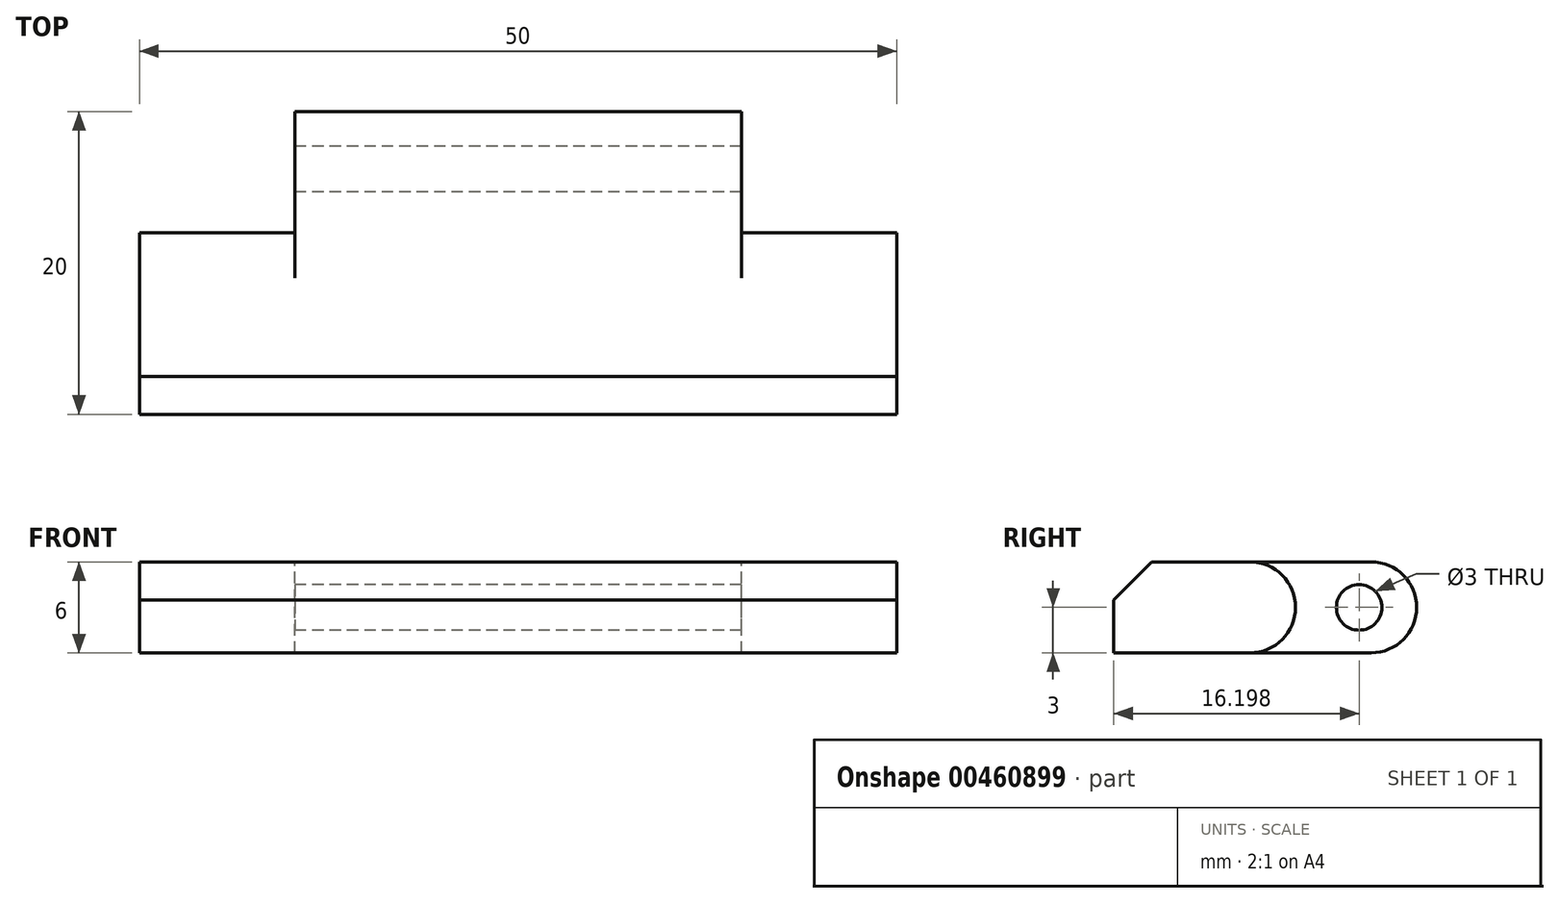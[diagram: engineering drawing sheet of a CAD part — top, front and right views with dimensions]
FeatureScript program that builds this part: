
annotation { "Feature Type Name" : "Feature", "Feature Type Description" : "" }
export const myFeature = defineFeature(function(context is Context, id is Id, definition is map)
    precondition{}
    {
        {
            var Q0;
            Q0=qCreatedBy(makeId("Top.planeOp"),FACE);
            var sketch = newSketch(context, id + "F0", { "sketchPlane" : qUnion([Q0])});
            skLineSegment(sketch, "E0.top", {"start": v(0, -17.76) * mm, "end": v(50, -17.76) * mm});
            skLineSegment(sketch, "E1", {"start": v(10.25, 2.24) * mm, "end": v(10.25, -5.76) * mm});
            skLineSegment(sketch, "E2", {"start": v(10.25, -5.76) * mm, "end": v(0, -5.76) * mm});
            skLineSegment(sketch, "E3", {"start": v(0, -5.76) * mm, "end": v(0, -17.76) * mm});
            skLineSegment(sketch, "E4", {"start": v(10.25, 2.24) * mm, "end": v(39.75, 2.24) * mm});
            skLineSegment(sketch, "E5", {"start": v(39.75, 2.24) * mm, "end": v(39.75, -5.76) * mm});
            skLineSegment(sketch, "E6", {"start": v(39.75, -5.76) * mm, "end": v(50, -5.76) * mm});
            skLineSegment(sketch, "E7", {"start": v(50, -5.76) * mm, "end": v(50, -17.76) * mm});
            skSolve(sketch);
        }
        {
            var Q0;
            Q0=makeQuery(id+"F0.imprint","IMPRINT",FACE,{"disambiguationData":[TD([[makeQuery(id+"F0.imprint","IMPRINT",EDGE,{"derivedFrom":sQuery(id+"F0.wireOp",EDGE,"E0.top")}),1.0]])]});
            extrude(context, id + "F1", {"entities" : qUnion([Q0]), "depth" : 6 * mm});
        }
        {
            var Q0;
            Q0=makeQuery(id+"F1.opExtrude","CAP_EDGE",EDGE,{"disambiguationData":[OSD([sQuery(id+"F0.wireOp",EDGE,"E4")])],"isStart":false});
            var Q1;
            Q1=makeQuery(id+"F1.opExtrude","CAP_EDGE",EDGE,{"disambiguationData":[OSD([sQuery(id+"F0.wireOp",EDGE,"E4")])],"isStart":true});
            var Q2;
            Q2=makeQuery(id+"F1.opExtrude","CAP_EDGE",EDGE,{"disambiguationData":[OSD([sQuery(id+"F0.wireOp",EDGE,"E2")])],"isStart":false});
            var Q3;
            Q3=makeQuery(id+"F1.opExtrude","CAP_EDGE",EDGE,{"disambiguationData":[OSD([sQuery(id+"F0.wireOp",EDGE,"E6")])],"isStart":false});
            var Q4;
            Q4=makeQuery(id+"F1.opExtrude","CAP_EDGE",EDGE,{"disambiguationData":[OSD([sQuery(id+"F0.wireOp",EDGE,"E2")])],"isStart":true});
            var Q5;
            Q5=makeQuery(id+"F1.opExtrude","CAP_EDGE",EDGE,{"disambiguationData":[OSD([sQuery(id+"F0.wireOp",EDGE,"E6")])],"isStart":true});
            fillet(context, id + "F2", {"entities" : qUnion([Q0, Q1, Q2, Q3, Q4, Q5]), "radius" : 3 * mm, "tangentPropagation" : true, "allowEdgeOverflow" : false});
        }
        {
            var Q0;
            Q0=makeQuery(id+"F1.opExtrude","SWEPT_FACE",FACE,{"disambiguationData":[OSD([sQuery(id+"F0.wireOp",EDGE,"E1")])]});
            var sketch = newSketch(context, id + "F3", { "sketchPlane" : qUnion([Q0])});
            skCircle(sketch, "E8", {"center": v(1.56, 3) * mm, "radius": 1.5 * mm});
            skSolve(sketch);
        }
        {
            var Q0;
            Q0=makeQuery(id+"F3.imprint","IMPRINT",FACE,{"disambiguationData":[TD([[makeQuery(id+"F3.imprint","IMPRINT",EDGE,{"derivedFrom":sQuery(id+"F3.wireOp",EDGE,"E8")}),1.0]])]});
            extrude(context, id + "F4", {"entities" : qUnion([Q0]), "operationType" : NewBodyOperationType.REMOVE, "endBound" : BoundingType.THROUGH_ALL, "oppositeDirection" : true, "depth" : 25 * mm});
        }
        {
            var Q0;
            Q0=makeQuery(id+"F1.opExtrude","CAP_EDGE",EDGE,{"disambiguationData":[OSD([sQuery(id+"F0.wireOp",EDGE,"E0.top")])],"isStart":false});
            chamfer(context, id + "F5", {"entities" : qUnion([Q0]), "width" : 2.5 * mm, "tangentPropagation" : true});
        }
    });
